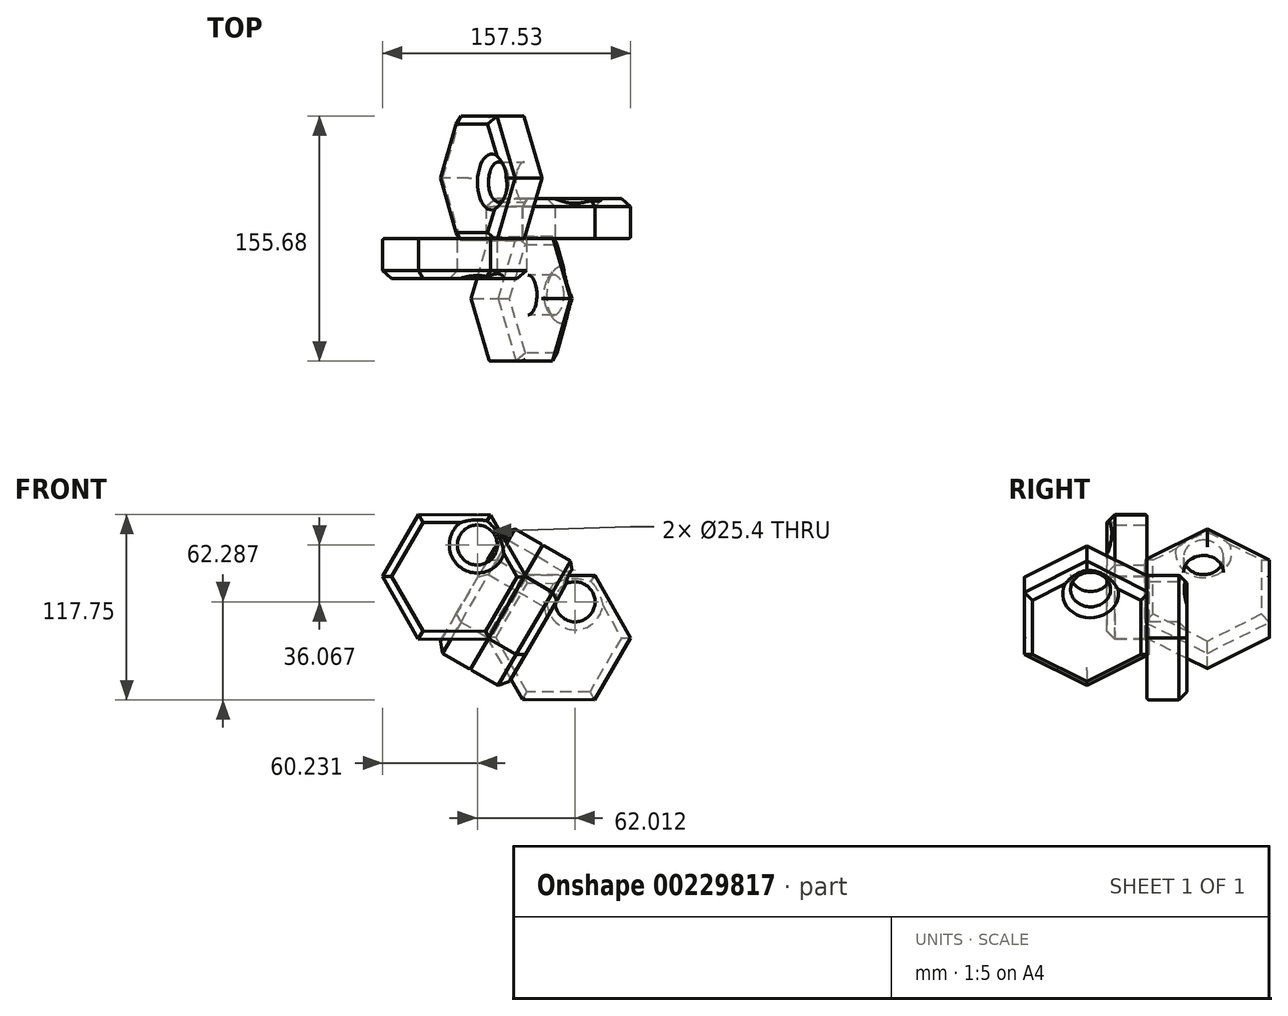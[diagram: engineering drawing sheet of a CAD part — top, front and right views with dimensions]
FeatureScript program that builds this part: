
annotation { "Feature Type Name" : "Feature", "Feature Type Description" : "" }
export const myFeature = defineFeature(function(context is Context, id is Id, definition is map)
    precondition{}
    {
        {
            var Q0;
            Q0=qCreatedBy(makeId("Front.planeOp"),FACE);
            var sketch = newSketch(context, id + "F0", { "sketchPlane" : qUnion([Q0])});
            skCircle(sketch, "E0.cCircle", {"center": v(0, 0) * mm, "radius": 39.55 * mm, "construction": true});
            skLineSegment(sketch, "E0.0", {"start": v(45.67, -0.15) * mm, "end": v(22.71, -39.63) * mm});
            skLineSegment(sketch, "E0.1", {"start": v(22.71, -39.63) * mm, "end": v(-22.96, -39.48) * mm});
            skLineSegment(sketch, "E0.2", {"start": v(-22.96, -39.48) * mm, "end": v(-45.67, 0.15) * mm});
            skLineSegment(sketch, "E0.3", {"start": v(-45.67, 0.15) * mm, "end": v(-22.71, 39.63) * mm});
            skLineSegment(sketch, "E0.4", {"start": v(-22.71, 39.63) * mm, "end": v(22.96, 39.48) * mm});
            skLineSegment(sketch, "E0.5", {"start": v(22.96, 39.48) * mm, "end": v(45.67, -0.15) * mm});
            skPoint(sketch, "E0.0.midPoint", {"position": v(34.2, -19.89) * mm});
            skSolve(sketch);
        }
        {
            var Q0;
            Q0 = qSketchRegion(id + "F0", true);
            extrude(context, id + "F1", {"entities" : qUnion([Q0]), "depth" : 25.4 * mm});
        }
        {
            var Q0;
            Q0=makeQuery(id+"F1.opExtrude","CAP_FACE",FACE,{"disambiguationData":[OSD([sQuery(id+"F0.wireOp",EDGE,"E0.0"),sQuery(id+"F0.wireOp",EDGE,"E0.1"),sQuery(id+"F0.wireOp",EDGE,"E0.2"),sQuery(id+"F0.wireOp",EDGE,"E0.3"),sQuery(id+"F0.wireOp",EDGE,"E0.4"),sQuery(id+"F0.wireOp",EDGE,"E0.5")])],"isStart":false});
            var sketch = newSketch(context, id + "F2", { "sketchPlane" : qUnion([Q0])});
            skCircle(sketch, "E1", {"center": v(10.38, 22.66) * mm, "radius": 7.3 * mm});
            skSolve(sketch);
        }
        {
            var Q0;
            Q0=sQuery(id+"F2.wireOp",VERTEX,"E1.center");
            var Q1;
            Q1=makeQuery(id+"F1.opExtrude","SWEPT_BODY",BODY,{"disambiguationData":[OSD([sQuery(id+"F0.wireOp",EDGE,"E0.0"),sQuery(id+"F0.wireOp",EDGE,"E0.1"),sQuery(id+"F0.wireOp",EDGE,"E0.2"),sQuery(id+"F0.wireOp",EDGE,"E0.3"),sQuery(id+"F0.wireOp",EDGE,"E0.4"),sQuery(id+"F0.wireOp",EDGE,"E0.5")])]});
            hole(context, id + "F3", {"style" : HoleStyle.SIMPLE, "endStyle" : HoleEndStyle.THROUGH, "holeDiameter" : 25.4 * mm, "locations" : qUnion([Q0]), "scope" : qUnion([Q1]), "isTappedThrough" : true});
        }
        {
            var Q0;
            Q0=makeQuery(id+"F1.opExtrude","CAP_FACE",FACE,{"disambiguationData":[OSD([sQuery(id+"F0.wireOp",EDGE,"E0.0"),sQuery(id+"F0.wireOp",EDGE,"E0.1"),sQuery(id+"F0.wireOp",EDGE,"E0.2"),sQuery(id+"F0.wireOp",EDGE,"E0.3"),sQuery(id+"F0.wireOp",EDGE,"E0.4"),sQuery(id+"F0.wireOp",EDGE,"E0.5")])],"isStart":false});
            fillet(context, id + "F4", {"entities" : qUnion([Q0]), "radius" : 1.27 * mm, "tangentPropagation" : true, "allowEdgeOverflow" : false});
        }
        {
            var Q0;
            Q0=makeQuery(id+"F1.opExtrude","CAP_FACE",FACE,{"disambiguationData":[OSD([sQuery(id+"F0.wireOp",EDGE,"E0.0"),sQuery(id+"F0.wireOp",EDGE,"E0.1"),sQuery(id+"F0.wireOp",EDGE,"E0.2"),sQuery(id+"F0.wireOp",EDGE,"E0.3"),sQuery(id+"F0.wireOp",EDGE,"E0.4"),sQuery(id+"F0.wireOp",EDGE,"E0.5")])],"isStart":true});
            chamfer(context, id + "F5", {"entities" : qUnion([Q0]), "width" : 5.08 * mm, "tangentPropagation" : true});
        }
        {
            var Q0;
            Q0=makeQuery(id+"F1.opExtrude","SWEPT_BODY",BODY,{"disambiguationData":[OSD([sQuery(id+"F0.wireOp",EDGE,"E0.0"),sQuery(id+"F0.wireOp",EDGE,"E0.1"),sQuery(id+"F0.wireOp",EDGE,"E0.2"),sQuery(id+"F0.wireOp",EDGE,"E0.3"),sQuery(id+"F0.wireOp",EDGE,"E0.4"),sQuery(id+"F0.wireOp",EDGE,"E0.5")])]});
            var Q1;
            {var subQ0=sQuery(id+"F0.wireOp",EDGE,"E0.3");Q1=makeQuery(id+"F4.opFillet","BLEND_EDGE",EDGE,{"blendedFrom":[makeQuery(id+"F1.opExtrude","CAP_EDGE",EDGE,{"disambiguationData":[OSD([subQ0])],"isStart":false}),makeQuery(id+"F1.opExtrude","CAP_FACE",FACE,{"disambiguationData":[OSD([sQuery(id+"F0.wireOp",EDGE,"E0.0"),sQuery(id+"F0.wireOp",EDGE,"E0.1"),sQuery(id+"F0.wireOp",EDGE,"E0.2"),subQ0,sQuery(id+"F0.wireOp",EDGE,"E0.4"),sQuery(id+"F0.wireOp",EDGE,"E0.5")])],"isStart":false})],"blendedInto":[makeQuery(id+"F1.opExtrude","CAP_FACE",FACE,{"disambiguationData":[OSD([sQuery(id+"F0.wireOp",EDGE,"E0.0"),sQuery(id+"F0.wireOp",EDGE,"E0.1"),sQuery(id+"F0.wireOp",EDGE,"E0.2"),subQ0,sQuery(id+"F0.wireOp",EDGE,"E0.4"),sQuery(id+"F0.wireOp",EDGE,"E0.5")])],"isStart":false})]});}
            circularPattern(context, id + "F6", {"entities" : qUnion([Q0]), "axis" : qUnion([Q1]), "angle" : 360 * degree, "instanceCount" : 4, "equalSpace" : true});
        }
    });
